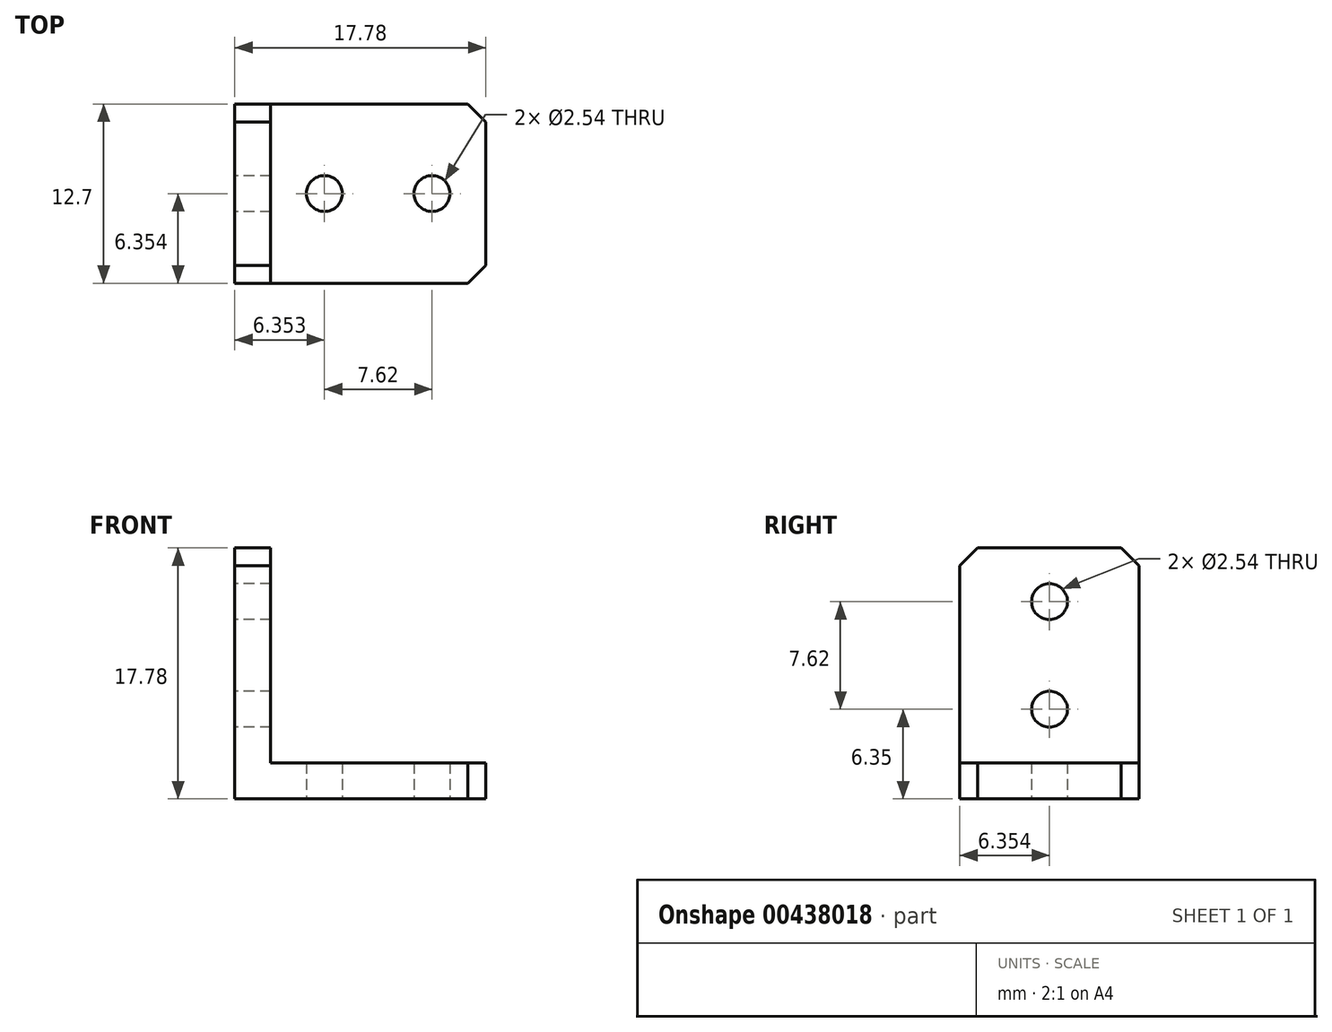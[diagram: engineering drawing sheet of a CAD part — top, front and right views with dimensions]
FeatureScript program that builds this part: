
annotation { "Feature Type Name" : "Feature", "Feature Type Description" : "" }
export const myFeature = defineFeature(function(context is Context, id is Id, definition is map)
    precondition{}
    {
        {
            var Q0;
            Q0=qCreatedBy(makeId("Top.planeOp"),FACE);
            var sketch = newSketch(context, id + "F0", { "sketchPlane" : qUnion([Q0])});
            skLineSegment(sketch, "E0.bottom", {"start": v(-34.97, 31.94) * mm, "end": v(-17.19, 31.94) * mm});
            skLineSegment(sketch, "E0.top", {"start": v(-34.97, 19.24) * mm, "end": v(-17.19, 19.24) * mm});
            skLineSegment(sketch, "E0.left", {"start": v(-34.97, 31.94) * mm, "end": v(-34.97, 19.24) * mm});
            skLineSegment(sketch, "E0.right", {"start": v(-17.19, 31.94) * mm, "end": v(-17.19, 19.24) * mm});
            skCircle(sketch, "E1", {"center": v(-21, 25.6) * mm, "radius": 1.27 * mm});
            skPoint(sketch, "E1.centerSnap0", {"position": v(-17.19, 25.6) * mm});
            skCircle(sketch, "E2", {"center": v(-28.62, 25.6) * mm, "radius": 1.27 * mm});
            skSolve(sketch);
        }
        {
            var Q0;
            Q0=makeQuery(id+"F0.imprint","IMPRINT",FACE,{"disambiguationData":[TD([[makeQuery(id+"F0.imprint","IMPRINT",EDGE,{"derivedFrom":sQuery(id+"F0.wireOp",EDGE,"E0.bottom")}),-1.0]])]});
            extrude(context, id + "F1", {"entities" : qUnion([Q0]), "depth" : 2.54 * mm});
        }
        {
            var Q0;
            Q0=makeQuery(id+"F1.opExtrude","CAP_FACE",FACE,{"disambiguationData":[OSD([sQuery(id+"F0.wireOp",EDGE,"E0.bottom"),sQuery(id+"F0.wireOp",EDGE,"E0.top"),sQuery(id+"F0.wireOp",EDGE,"E0.left"),sQuery(id+"F0.wireOp",EDGE,"E0.right")])],"isStart":false});
            var sketch = newSketch(context, id + "F2", { "sketchPlane" : qUnion([Q0])});
            skLineSegment(sketch, "E3.bottom", {"start": v(-34.97, 31.94) * mm, "end": v(-32.43, 31.94) * mm});
            skLineSegment(sketch, "E3.top", {"start": v(-34.97, 19.24) * mm, "end": v(-32.43, 19.24) * mm});
            skLineSegment(sketch, "E3.left", {"start": v(-34.97, 31.94) * mm, "end": v(-34.97, 19.24) * mm});
            skLineSegment(sketch, "E3.right", {"start": v(-32.43, 31.94) * mm, "end": v(-32.43, 19.24) * mm});
            skSolve(sketch);
        }
        {
            var Q0;
            Q0=makeQuery(id+"F2.imprint","IMPRINT",FACE,{"disambiguationData":[TD([[makeQuery(id+"F2.imprint","IMPRINT",EDGE,{"derivedFrom":sQuery(id+"F2.wireOp",EDGE,"E3.bottom")}),-1.0]])]});
            extrude(context, id + "F3", {"entities" : qUnion([Q0]), "operationType" : NewBodyOperationType.ADD, "depth" : 15.24 * mm});
        }
        {
            var Q0;
            Q0=makeQuery(id+"F3.boolean.opBoolean","MERGE",FACE,{"derivedFrom":[makeQuery(id+"F1.opExtrude","SWEPT_FACE",FACE,{"disambiguationData":[OSD([sQuery(id+"F0.wireOp",EDGE,"E0.left")])]}),makeQuery(id+"F3.opExtrude","SWEPT_FACE",FACE,{"disambiguationData":[OSD([sQuery(id+"F2.wireOp",EDGE,"E3.left")])]})]});
            var sketch = newSketch(context, id + "F4", { "sketchPlane" : qUnion([Q0])});
            skCircle(sketch, "E4", {"center": v(-25.6, 13.97) * mm, "radius": 1.27 * mm});
            skPoint(sketch, "E4.centerSnap0", {"position": v(-25.6, 17.78) * mm});
            skCircle(sketch, "E5", {"center": v(-25.6, 6.35) * mm, "radius": 1.27 * mm});
            skSolve(sketch);
        }
        {
            var Q0;
            Q0=qSketchRegion(id+"F4",true);
            extrude(context, id + "F5", {"entities" : qUnion([Q0]), "operationType" : NewBodyOperationType.REMOVE, "oppositeDirection" : true, "depth" : 25.4 * mm});
        }
        {
            var Q0;
            Q0=makeQuery(id+"F3.opExtrude","CAP_EDGE",EDGE,{"disambiguationData":[OSD([sQuery(id+"F2.wireOp",EDGE,"E3.top")])],"isStart":false});
            var Q1;
            Q1=makeQuery(id+"F3.opExtrude","CAP_EDGE",EDGE,{"disambiguationData":[OSD([sQuery(id+"F2.wireOp",EDGE,"E3.bottom")])],"isStart":false});
            var Q2;
            Q2=makeQuery(id+"F1.opExtrude","SWEPT_EDGE",EDGE,{"disambiguationData":[OSD([sQuery(id+"F0.wireOp",EDGE,"E0.top"),sQuery(id+"F0.wireOp",EDGE,"E0.right")])]});
            var Q3;
            Q3=makeQuery(id+"F1.opExtrude","SWEPT_EDGE",EDGE,{"disambiguationData":[OSD([sQuery(id+"F0.wireOp",EDGE,"E0.bottom"),sQuery(id+"F0.wireOp",EDGE,"E0.right")])]});
            chamfer(context, id + "F6", {"entities" : qUnion([Q0, Q1, Q2, Q3]), "width" : 1.27 * mm, "tangentPropagation" : true});
        }
    });
